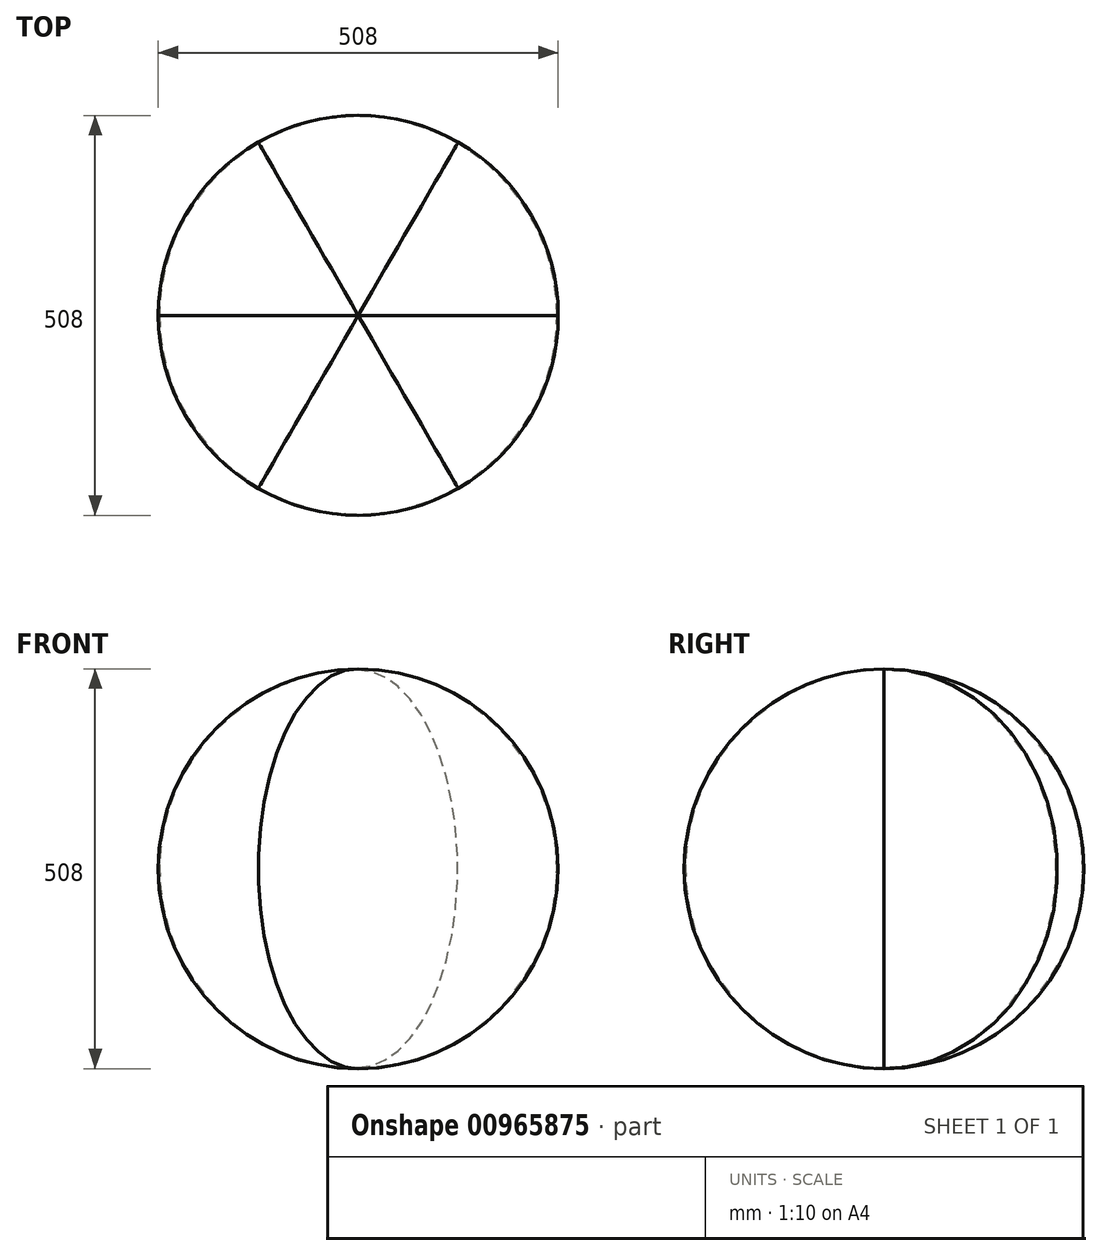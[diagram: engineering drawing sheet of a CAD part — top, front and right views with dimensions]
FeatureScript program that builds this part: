
annotation { "Feature Type Name" : "Feature", "Feature Type Description" : "" }
export const myFeature = defineFeature(function(context is Context, id is Id, definition is map)
    precondition{}
    {
        {
            var Q0;
            Q0=qCreatedBy(makeId("Front.planeOp"),FACE);
            var sketch = newSketch(context, id + "F0", { "sketchPlane" : qUnion([Q0])});
            skArc(sketch, "E0", {"start": v(0, -254) * mm, "mid": v(254, 0) * mm, "end": v(0, 254) * mm});
            skArc(sketch, "E1", {"start": v(0, -252.41) * mm, "mid": v(252.41, 0) * mm, "end": v(0, 252.41) * mm});
            skLineSegment(sketch, "E2", {"start": v(0, 254) * mm, "end": v(0, -252.41) * mm});
            skLineSegment(sketch, "E3", {"start": v(0, -252.41) * mm, "end": v(0, -254) * mm});
            skSolve(sketch);
        }
        {
            var Q0;
            {var subQ0=sQuery(id+"F0.wireOp",EDGE,"E0");Q0=makeQuery(id+"F0.imprint","IMPRINT",FACE,{"disambiguationData":[TD([[makeQuery(id+"F0.imprint","IMPRINT",EDGE,{"derivedFrom":subQ0}),1.0]])]});}
            var Q1;
            Q1=sQuery(id+"F0.wireOp",EDGE,"E2");
            revolve(context, id + "F1", {"surfaceOperationType" : NewSurfaceOperationType.NEW, "entities" : qUnion([Q0]), "axis" : qUnion([Q1]), "revolveType" : RevolveType.ONE_DIRECTION, "angle" : 60 * degree});
        }
        {
            var Q0;
            Q0=qCreatedBy(makeId("Right.planeOp"),FACE);
            var sketch = newSketch(context, id + "F2", { "sketchPlane" : qUnion([Q0])});
            skLineSegment(sketch, "E4", {"start": v(0, 254.3) * mm, "end": v(0, -248.58) * mm});
            skSolve(sketch);
        }
        {
            var Q0;
            Q0=makeQuery(id+"F1.opRevolve","SWEPT_BODY",BODY,{"disambiguationData":[OSD([sQuery(id+"F0.wireOp",EDGE,"E0"),sQuery(id+"F0.wireOp",EDGE,"E1"),sQuery(id+"F0.wireOp",EDGE,"E2"),sQuery(id+"F0.wireOp",EDGE,"E3")])]});
            var Q1;
            Q1=sQuery(id+"F2.wireOp",EDGE,"E4");
            circularPattern(context, id + "F3", {"entities" : qUnion([Q0]), "axis" : qUnion([Q1]), "angle" : 360 * degree, "instanceCount" : 6, "equalSpace" : true});
        }
    });
